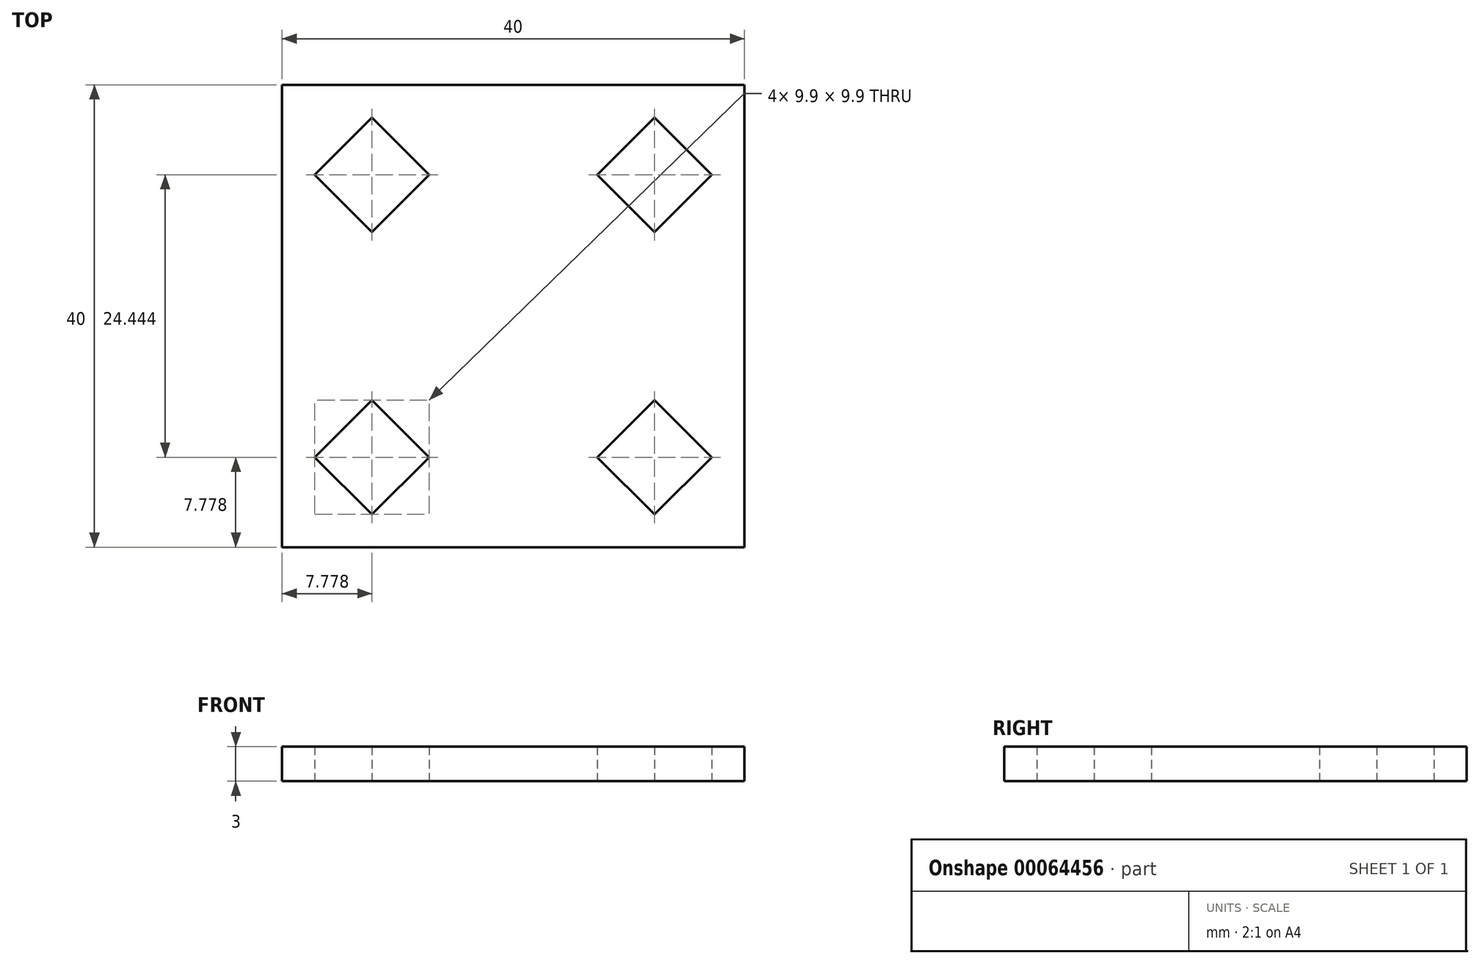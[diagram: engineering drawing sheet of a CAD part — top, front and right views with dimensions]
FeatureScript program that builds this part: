
annotation { "Feature Type Name" : "Feature", "Feature Type Description" : "" }
export const myFeature = defineFeature(function(context is Context, id is Id, definition is map)
    precondition{}
    {
        {
            var Q0;
            Q0=qCreatedBy(makeId("Top.planeOp"),FACE);
            var sketch = newSketch(context, id + "F0", { "sketchPlane" : qUnion([Q0])});
            skLineSegment(sketch, "E0.bottom", {"start": v(-20, 20) * mm, "end": v(20, 20) * mm});
            skLineSegment(sketch, "E0.top", {"start": v(-20, -20) * mm, "end": v(20, -20) * mm});
            skLineSegment(sketch, "E0.left", {"start": v(-20, 20) * mm, "end": v(-20, -20) * mm});
            skLineSegment(sketch, "E0.right", {"start": v(20, 20) * mm, "end": v(20, -20) * mm});
            skLineSegment(sketch, "E1", {"start": v(0, 0) * mm, "end": v(-20, 0) * mm, "construction": true});
            skLineSegment(sketch, "E2", {"start": v(0, 0) * mm, "end": v(0, 20) * mm, "construction": true});
            skLineSegment(sketch, "E3", {"start": v(-17.17, 12.22) * mm, "end": v(-12.22, 17.17) * mm});
            skLineSegment(sketch, "E4", {"start": v(-12.22, 17.17) * mm, "end": v(-7.27, 12.22) * mm});
            skLineSegment(sketch, "E5", {"start": v(-7.27, 12.22) * mm, "end": v(-12.22, 7.27) * mm});
            skLineSegment(sketch, "E6", {"start": v(-12.22, 7.27) * mm, "end": v(-17.17, 12.22) * mm});
            skLineSegment(sketch, "E7", {"start": v(-20, 20) * mm, "end": v(0, 0) * mm, "construction": true});
            skLineSegment(sketch, "E8", {"start": v(-9.75, 14.7) * mm, "end": v(-14.7, 9.75) * mm, "construction": true});
            skLineSegment(sketch, "E9", {"start": v(-9.75, 9.75) * mm, "end": v(-14.7, 14.7) * mm, "construction": true});
            skPoint(sketch, "E10", {"position": v(-12.22, 12.22) * mm});
            skLineSegment(sketch, "E11.1.0", {"start": v(-7.27, -12.22) * mm, "end": v(-12.22, -17.17) * mm});
            skLineSegment(sketch, "E11.1.1", {"start": v(-12.22, -7.27) * mm, "end": v(-7.27, -12.22) * mm});
            skLineSegment(sketch, "E11.1.2", {"start": v(-17.17, -12.22) * mm, "end": v(-12.22, -7.27) * mm});
            skLineSegment(sketch, "E11.1.3", {"start": v(-12.22, -17.17) * mm, "end": v(-17.17, -12.22) * mm});
            skLineSegment(sketch, "E11.2.0", {"start": v(12.22, -7.27) * mm, "end": v(17.17, -12.22) * mm});
            skLineSegment(sketch, "E11.2.1", {"start": v(7.27, -12.22) * mm, "end": v(12.22, -7.27) * mm});
            skLineSegment(sketch, "E11.2.2", {"start": v(12.22, -17.17) * mm, "end": v(7.27, -12.22) * mm});
            skLineSegment(sketch, "E11.2.3", {"start": v(17.17, -12.22) * mm, "end": v(12.22, -17.17) * mm});
            skPoint(sketch, "E11.center", {"position": v(0, 0) * mm});
            skLineSegment(sketch, "E12.2.3.0", {"start": v(7.27, 12.22) * mm, "end": v(12.22, 17.17) * mm});
            skLineSegment(sketch, "E12.3.3.0", {"start": v(12.22, 7.27) * mm, "end": v(7.27, 12.22) * mm});
            skLineSegment(sketch, "E12.6.3.0", {"start": v(17.17, 12.22) * mm, "end": v(12.22, 7.27) * mm});
            skLineSegment(sketch, "E12.9.3.0", {"start": v(12.22, 17.17) * mm, "end": v(17.17, 12.22) * mm});
            skSolve(sketch);
        }
        {
            var Q0;
            Q0 = qSketchRegion(id + "F0", true);
            extrude(context, id + "F1", {"entities" : qUnion([Q0]), "depth" : 3 * mm});
        }
    });
